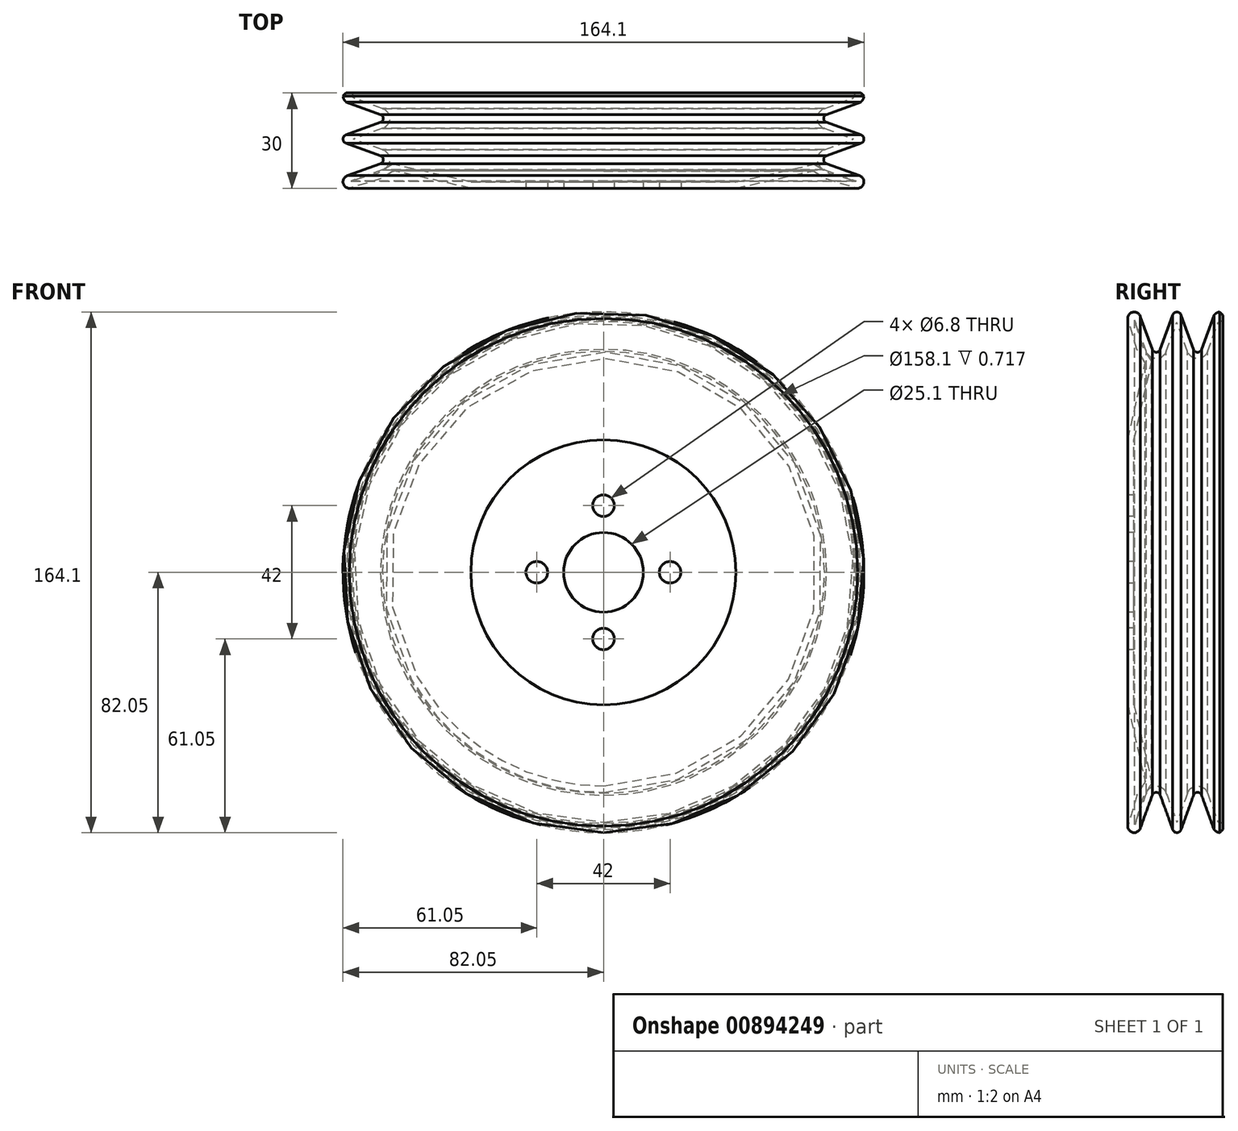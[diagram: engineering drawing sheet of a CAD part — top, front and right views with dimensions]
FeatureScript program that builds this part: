
annotation { "Feature Type Name" : "Feature", "Feature Type Description" : "" }
export const myFeature = defineFeature(function(context is Context, id is Id, definition is map)
    precondition{}
    {
        {
            var Q0;
            Q0=qCreatedBy(makeId("Right.planeOp"),FACE);
            var sketch = newSketch(context, id + "F0", { "sketchPlane" : qUnion([Q0])});
            skLineSegment(sketch, "E0", {"start": v(2, 12.55) * mm, "end": v(2, 41.74) * mm});
            skLineSegment(sketch, "E1", {"start": v(0, 41.74) * mm, "end": v(5.45, 65.85) * mm});
            skLineSegment(sketch, "E2", {"start": v(5.4, 66.22) * mm, "end": v(3.04, 70) * mm});
            skArc(sketch, "E3", {"start": v(5.45, 65.85) * mm, "mid": v(5.46, 66.04) * mm, "end": v(5.4, 66.22) * mm});
            skLineSegment(sketch, "E4", {"start": v(0, 80.05) * mm, "end": v(2.98, 70.11) * mm});
            skArc(sketch, "E5", {"start": v(2.98, 70.11) * mm, "mid": v(3, 70.05) * mm, "end": v(3.04, 70) * mm});
            skLineSegment(sketch, "E6", {"start": v(2, 41.74) * mm, "end": v(7.55, 66.27) * mm});
            skLineSegment(sketch, "E7", {"start": v(7.49, 66.65) * mm, "end": v(4.87, 70.83) * mm});
            skArc(sketch, "E8", {"start": v(7.55, 66.27) * mm, "mid": v(7.56, 66.46) * mm, "end": v(7.49, 66.65) * mm});
            skLineSegment(sketch, "E9", {"start": v(4.82, 70.95) * mm, "end": v(2.25, 79.51) * mm});
            skArc(sketch, "E10", {"start": v(4.82, 70.95) * mm, "mid": v(4.84, 70.88) * mm, "end": v(4.87, 70.83) * mm});
            skLineSegment(sketch, "E11", {"start": v(14.18, 81.05) * mm, "end": v(10.25, 70.26) * mm});
            skLineSegment(sketch, "E12", {"start": v(4, 80.55) * mm, "end": v(7.75, 70.26) * mm});
            skLineSegment(sketch, "E13", {"start": v(27.18, 81.05) * mm, "end": v(23.25, 70.26) * mm});
            skLineSegment(sketch, "E14", {"start": v(16.82, 81.05) * mm, "end": v(20.75, 70.26) * mm});
            skArc(sketch, "E15", {"start": v(16.82, 81.05) * mm, "mid": v(15.5, 82.05) * mm, "end": v(14.18, 81.05) * mm});
            skArc(sketch, "E16", {"start": v(4, 80.55) * mm, "mid": v(1.78, 82.03) * mm, "end": v(0, 80.05) * mm});
            skLineSegment(sketch, "E17", {"start": v(29, 82.05) * mm, "end": v(30, 81.05) * mm});
            skArc(sketch, "E18", {"start": v(29, 82.05) * mm, "mid": v(28, 81.73) * mm, "end": v(27.18, 81.05) * mm});
            skArc(sketch, "E19", {"start": v(7.75, 70.26) * mm, "mid": v(9, 69.35) * mm, "end": v(10.25, 70.26) * mm});
            skLineSegment(sketch, "E20", {"start": v(2.25, 79.51) * mm, "end": v(5.86, 69.6) * mm});
            skLineSegment(sketch, "E21", {"start": v(15.45, 78.7) * mm, "end": v(12.14, 69.6) * mm});
            skLineSegment(sketch, "E22", {"start": v(15.55, 78.7) * mm, "end": v(18.86, 69.6) * mm});
            skLineSegment(sketch, "E23", {"start": v(28.34, 78.4) * mm, "end": v(25.14, 69.6) * mm});
            skArc(sketch, "E24", {"start": v(5.86, 69.6) * mm, "mid": v(9, 67.35) * mm, "end": v(12.14, 69.6) * mm});
            skArc(sketch, "E25", {"start": v(15.55, 78.7) * mm, "mid": v(15.5, 78.73) * mm, "end": v(15.45, 78.7) * mm});
            skLineSegment(sketch, "E26", {"start": v(30, 79.05) * mm, "end": v(29.28, 79.05) * mm});
            skArc(sketch, "E27", {"start": v(29.28, 79.05) * mm, "mid": v(28.7, 78.87) * mm, "end": v(28.34, 78.4) * mm});
            skArc(sketch, "E28", {"start": v(20.75, 70.26) * mm, "mid": v(22, 69.35) * mm, "end": v(23.25, 70.26) * mm});
            skArc(sketch, "E29", {"start": v(18.86, 69.6) * mm, "mid": v(22, 67.35) * mm, "end": v(25.14, 69.6) * mm});
            skLineSegment(sketch, "E30", {"start": v(30, 81.05) * mm, "end": v(30, 79.05) * mm});
            skLineSegment(sketch, "E31", {"start": v(0, 41.74) * mm, "end": v(0, 12.55) * mm});
            skLineSegment(sketch, "E32", {"start": v(0, 12.55) * mm, "end": v(2, 12.55) * mm});
            skLineSegment(sketch, "E33", {"start": v(0, 0) * mm, "end": v(0, 12.55) * mm, "construction": true});
            skLineSegment(sketch, "E34", {"start": v(0, 0) * mm, "end": v(30, 0) * mm});
            skSolve(sketch);
        }
        {
            var Q0;
            Q0 = qSketchRegion(id + "F0", true);
            var Q1;
            Q1=sQuery(id+"F0.wireOp",EDGE,"E34");
            revolve(context, id + "F1", {"surfaceOperationType" : NewSurfaceOperationType.NEW, "entities" : qUnion([Q0]), "axis" : qUnion([Q1]), "revolveType" : RevolveType.FULL});
        }
        {
            var Q0;
            Q0=qCreatedBy(makeId("Front.planeOp"),FACE);
            var sketch = newSketch(context, id + "F2", { "sketchPlane" : qUnion([Q0])});
            skLineSegment(sketch, "E35", {"start": v(0, 21) * mm, "end": v(0, -21) * mm, "construction": true});
            skLineSegment(sketch, "E36", {"start": v(-21, 0) * mm, "end": v(21, 0) * mm, "construction": true});
            skCircle(sketch, "E37", {"center": v(0, 21) * mm, "radius": 3.4 * mm});
            skCircle(sketch, "E38", {"center": v(21, 0) * mm, "radius": 3.4 * mm});
            skCircle(sketch, "E39", {"center": v(0, -21) * mm, "radius": 3.4 * mm});
            skCircle(sketch, "E40", {"center": v(-21, 0) * mm, "radius": 3.4 * mm});
            skSolve(sketch);
        }
        {
            var Q0;
            Q0=makeQuery(id+"F2.imprint","IMPRINT",FACE,{"disambiguationData":[TD([[makeQuery(id+"F2.imprint","IMPRINT",EDGE,{"derivedFrom":sQuery(id+"F2.wireOp",EDGE,"E37")}),1.0]])]});
            var Q1;
            Q1=makeQuery(id+"F2.imprint","IMPRINT",FACE,{"disambiguationData":[TD([[makeQuery(id+"F2.imprint","IMPRINT",EDGE,{"derivedFrom":sQuery(id+"F2.wireOp",EDGE,"E38")}),1.0]])]});
            var Q2;
            Q2=makeQuery(id+"F2.imprint","IMPRINT",FACE,{"disambiguationData":[TD([[makeQuery(id+"F2.imprint","IMPRINT",EDGE,{"derivedFrom":sQuery(id+"F2.wireOp",EDGE,"E39")}),1.0]])]});
            var Q3;
            Q3=makeQuery(id+"F2.imprint","IMPRINT",FACE,{"disambiguationData":[TD([[makeQuery(id+"F2.imprint","IMPRINT",EDGE,{"derivedFrom":sQuery(id+"F2.wireOp",EDGE,"E40")}),1.0]])]});
            extrude(context, id + "F3", {"entities" : qUnion([Q0, Q1, Q2, Q3]), "operationType" : NewBodyOperationType.REMOVE, "endBound" : BoundingType.THROUGH_ALL, "oppositeDirection" : true, "depth" : 25 * mm, "offsetDistance" : 25 * mm});
        }
    });
